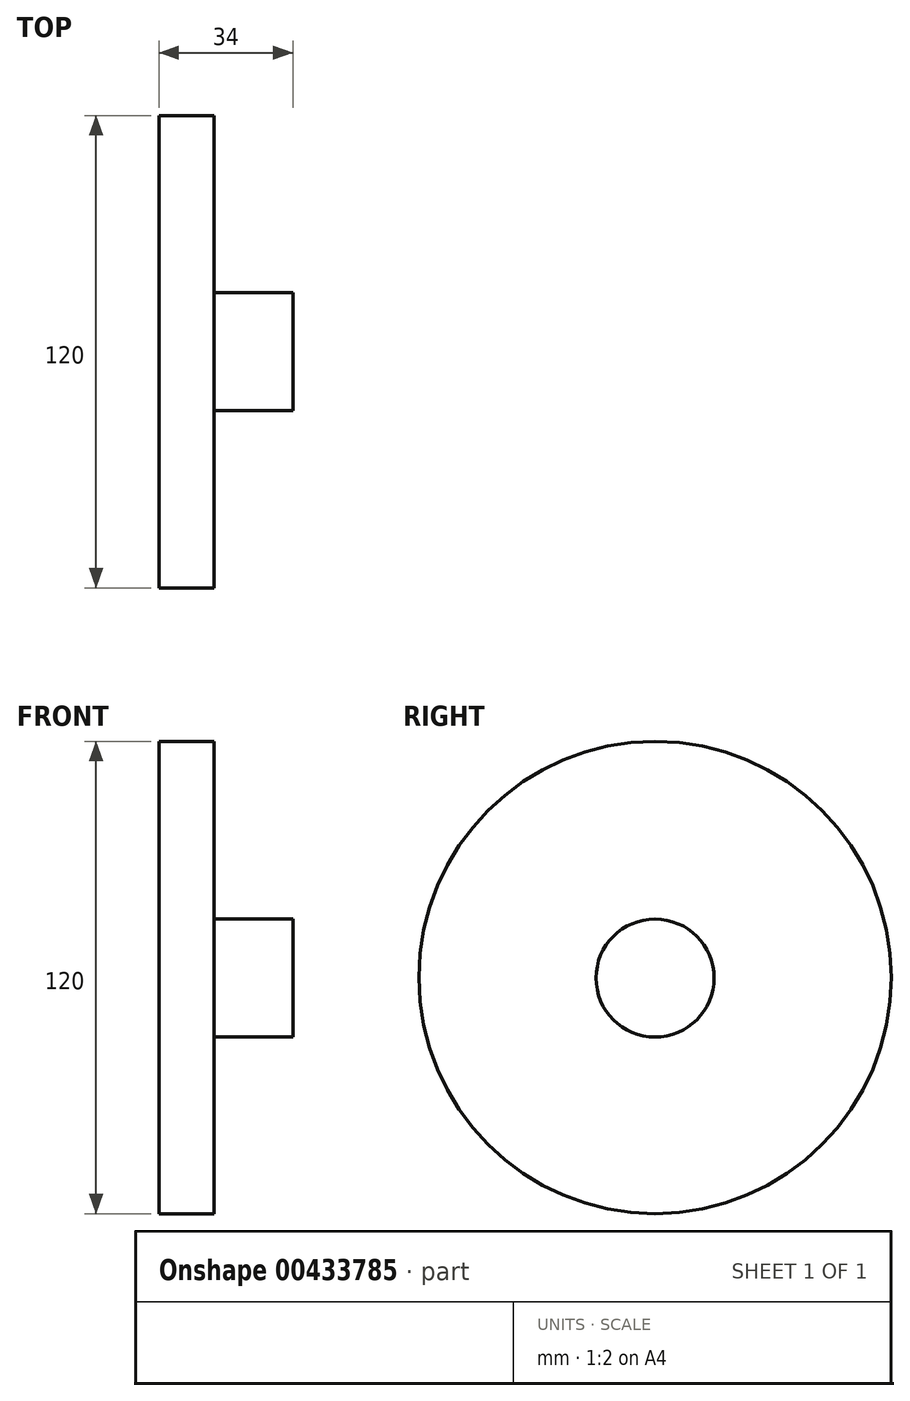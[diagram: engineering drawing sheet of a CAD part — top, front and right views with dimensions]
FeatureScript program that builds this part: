
annotation { "Feature Type Name" : "Feature", "Feature Type Description" : "" }
export const myFeature = defineFeature(function(context is Context, id is Id, definition is map)
    precondition{}
    {
        {
            var Q0;
            Q0=qCreatedBy(makeId("Right.planeOp"),FACE);
            var sketch = newSketch(context, id + "F0", { "sketchPlane" : qUnion([Q0])});
            skCircle(sketch, "E0", {"center": v(0, 0.15) * mm, "radius": 60 * mm});
            skSolve(sketch);
        }
        {
            var Q0;
            Q0=makeQuery(id+"F0.imprint","IMPRINT",FACE,{"disambiguationData":[TD([[makeQuery(id+"F0.imprint","IMPRINT",EDGE,{"derivedFrom":sQuery(id+"F0.wireOp",EDGE,"E0")}),1.0]])]});
            extrude(context, id + "F1", {"entities" : qUnion([Q0]), "depth" : 14 * mm});
        }
        {
            var Q0;
            Q0=makeQuery(id+"F1.opExtrude","CAP_FACE",FACE,{"disambiguationData":[OSD([sQuery(id+"F0.wireOp",EDGE,"E0")])],"isStart":false});
            var sketch = newSketch(context, id + "F2", { "sketchPlane" : qUnion([Q0])});
            skCircle(sketch, "E1", {"center": v(0, 0) * mm, "radius": 15 * mm});
            skSolve(sketch);
        }
        {
            var Q0;
            Q0=makeQuery(id+"F2.imprint","IMPRINT",FACE,{"disambiguationData":[TD([[makeQuery(id+"F2.imprint","IMPRINT",EDGE,{"derivedFrom":sQuery(id+"F2.wireOp",EDGE,"E1")}),1.0]])]});
            extrude(context, id + "F3", {"entities" : qUnion([Q0]), "operationType" : NewBodyOperationType.ADD, "depth" : 20 * mm});
        }
    });
